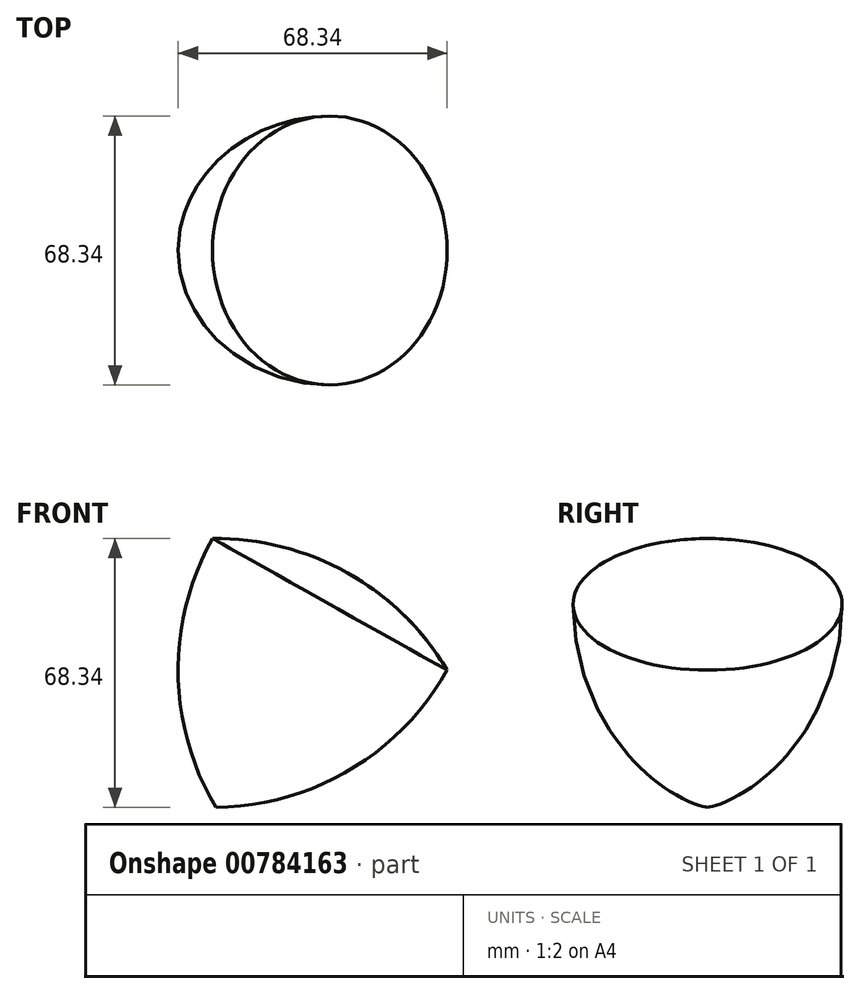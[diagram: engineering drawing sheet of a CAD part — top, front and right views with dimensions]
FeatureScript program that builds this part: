
annotation { "Feature Type Name" : "Feature", "Feature Type Description" : "" }
export const myFeature = defineFeature(function(context is Context, id is Id, definition is map)
    precondition{}
    {
        {
            var Q0;
            Q0=qCreatedBy(makeId("Front.planeOp"),FACE);
            var sketch = newSketch(context, id + "F0", { "sketchPlane" : qUnion([Q0])});
            skPoint(sketch, "E0.0.midPoint", {"position": v(9.65, 17.2) * mm});
            skArc(sketch, "E1", {"start": v(-19.3, -34.4) * mm, "mid": v(14.75, -24.83) * mm, "end": v(39.45, 0.49) * mm});
            skArc(sketch, "E2", {"start": v(-20.15, 33.92) * mm, "mid": v(-28.88, -0.36) * mm, "end": v(-19.3, -34.4) * mm});
            skArc(sketch, "E3", {"start": v(39.45, 0.49) * mm, "mid": v(14.13, 25.19) * mm, "end": v(-20.15, 33.92) * mm});
            skLineSegment(sketch, "E4", {"start": v(-19.3, -34.4) * mm, "end": v(14.13, 25.19) * mm});
            skSolve(sketch);
        }
        {
            var Q0;
            {var subQ0=sQuery(id+"F0.wireOp",EDGE,"E2");Q0=makeQuery(id+"F0.imprint","IMPRINT",FACE,{"disambiguationData":[TD([[makeQuery(id+"F0.imprint","IMPRINT",EDGE,{"derivedFrom":subQ0}),1.0]])]});}
            var Q1;
            Q1=sQuery(id+"F0.wireOp",EDGE,"E4");
            revolve(context, id + "F1", {"surfaceOperationType" : NewSurfaceOperationType.NEW, "entities" : qUnion([Q0]), "axis" : qUnion([Q1]), "revolveType" : RevolveType.FULL});
        }
    });
